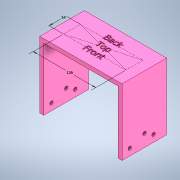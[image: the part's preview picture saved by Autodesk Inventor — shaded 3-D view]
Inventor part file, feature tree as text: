
AUTODESK INVENTOR PART (.ipt)
format: ipt  version: 2022.1 (Build 261234020, 234B)  size: 462,848 bytes
history: native  units: mm
features: sketch x6, extrude x2, hole x2, emboss x1
ambient origin geometry x8: Origin, YZ Plane, XZ Plane, XY Plane, X Axis, Y Axis, Z Axis, Center Point
bodies: Body1 (feature_tree)
feature tree (11):
  extrude  "Extrusion22"  Depth=166.0mm
  extrude  "Extrusion23"  TaperAngle=0.0deg  [1 undecoded]
  emboss  "Emboss1"
  hole  "Hole6"  [1 undecoded]
  hole  "Hole7"  [1 undecoded]
  sketch  "Sketch53"  dims[d230=25.0mm d231=6.756mm d232=6.0mm d233=12.878mm d234=2.0mm d235=14.3117mm d236=8.0mm d237=0.0mm d238=14.0mm d239=18.35mm d240=29.65mm d241=6.756mm d242=6.0mm d243=15.875mm d244=4.826mm d245=14.3117mm d246=9.53mm d247=20.594885mm d248=34.0mm d249=126.0mm d64=1.0mm d65=1.0mm d66=1.0mm d67=0.15mm d68=0.25mm d69=0.375mm d70=14.3117mm d71=0.75mm d72=20.594885mm d73=0.0625mm d74=0.75mm d75=0.375mm]
  sketch  "Sketch47"  dims[d218=90.0mm d219=166.0mm]
  sketch  "Sketch48"  dims[d220=8.0mm d221=0.0mm]
  sketch  "Sketch49"  dims[d222=8.0mm d223=8.0mm]
  sketch  "Sketch51"  dims[d224=126.0mm d225=0.0mm]
  sketch  "Sketch52"  dims[d226=1.0mm d227=0.0mm]
note: 3 required parameter values undecoded (feature->parameter linkage not recoverable at this tier; creation-order binding heuristic only, values carry confidence <= 0.55)
